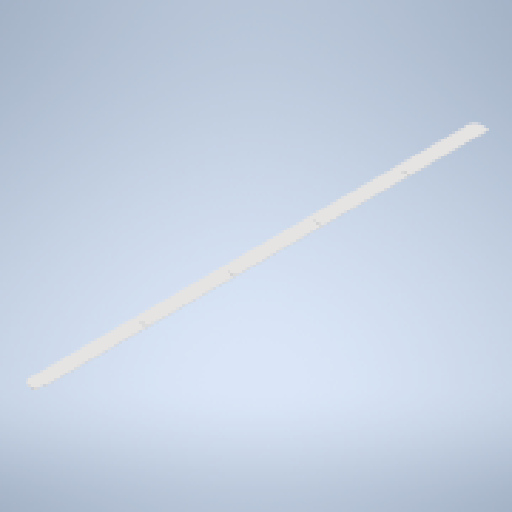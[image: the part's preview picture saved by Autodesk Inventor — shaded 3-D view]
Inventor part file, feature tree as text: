
AUTODESK INVENTOR PART (.ipt)
format: ipt  version: 2025 (Build 290162010, 162A)  size: 180,224 bytes
history: native  units: mm
features: sketch x2, sheet_metal_op x1, extrude x1, pattern_linear x1, chamfer x1, other x1
ambient origin geometry x8: Origin, YZ Plane, XZ Plane, XY Plane, X Axis, Y Axis, Z Axis, Center Point
bodies: Solid1 (feature_tree)
feature tree (7):
  sheet_metal_op  "Face1"
  extrude  "Extrusion1"  Depth=2900.463mm
  pattern_linear  "Rectangular Pattern1"  Spacing1=509.256mm  [1 undecoded]
  chamfer  "Corner Round1"
  sketch  "Sketch1"  dims[d0=95.0mm d1=2900.463mm]
  other  "Plate1"
  sketch  "Sketch2"  dims[d2=3.0mm d3=509.256mm d4=3.2mm d5=48.5mm d6=0.0mm d7=0.0mm d10=12.0mm d11=53.0mm d12=40.0mm d14=560.0mm d15=40.0mm]
note: 1 required parameter value undecoded (feature->parameter linkage not recoverable at this tier; creation-order binding heuristic only, values carry confidence <= 0.55)
